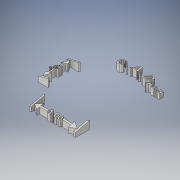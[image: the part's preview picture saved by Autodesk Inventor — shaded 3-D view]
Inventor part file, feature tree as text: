
AUTODESK INVENTOR PART (.ipt)
format: ipt  version: 2016 (Build 200138000, 138)  size: 753,664 bytes
history: native  units: in
note: dims shown in document units (in); Inventor stores cm internally (conversion verified against a paired STEP export)
features: reference x5, sketch x3, extrude x2, revolve x1, projected_geometry x1
ambient origin geometry x8: Origin, YZ Plane, XZ Plane, XY Plane, X Axis, Y Axis, Z Axis, Center Point
bodies: Solid1 (feature_tree)
feature tree (12):
  revolve  "Revolution1"  [1 undecoded]
  extrude  "Extrusion1"  Depth=0.1in
  extrude  "Extrusion2"  Depth=0.275in
  sketch  "Sketch1"  dims[d0=0.8265in d1=0.175in]
  sketch  "Sketch2"  dims[d2=0.05in d3=0.1in]
  projected_geometry  "Projected Loop1"
  reference  "Reference1"
  reference  "Reference2"
  reference  "Reference3"
  sketch  "Sketch3"  dims[d4=0.15in d5=0.275in d6=90.0deg d7=1.55in d9=1.0in d11=0.035in d13=1.0in d14=0.035in d15=0.0175in d16=0.6536in d17=0.0175in d18=0.15in d19=0.075in d20=0.05in d21=0.035in d22=0.0175in d23=0.325in d24=0.0175in d25=0.15in d26=0.3in d27=0.1in d28=0.035in d29=0.015in d30=0.015in d31=0.035in d32=0.0175in d33=0.225in d34=0.1in d35=1.1in d36=0.035in d38=60.0deg d39=0.025in d40=0.0in d41=0.0in d42=0.125in d43=0.125in d44=0.04in d45=0.05in d46=0.04in d47=0.04in d49=0.025in d50=0.125in d51=0.5in d52=0.085in d53=0.1in d54=0.975in d55=0.025in d56=0.9822in d57=0.9822in d58=15.0deg d59=0.04in d60=0.025in d61=0.5in d62=0.0in]
  reference  "Reference4"
  reference  "Reference5"
note: 1 required parameter value undecoded (feature->parameter linkage not recoverable at this tier; creation-order binding heuristic only, values carry confidence <= 0.55)
